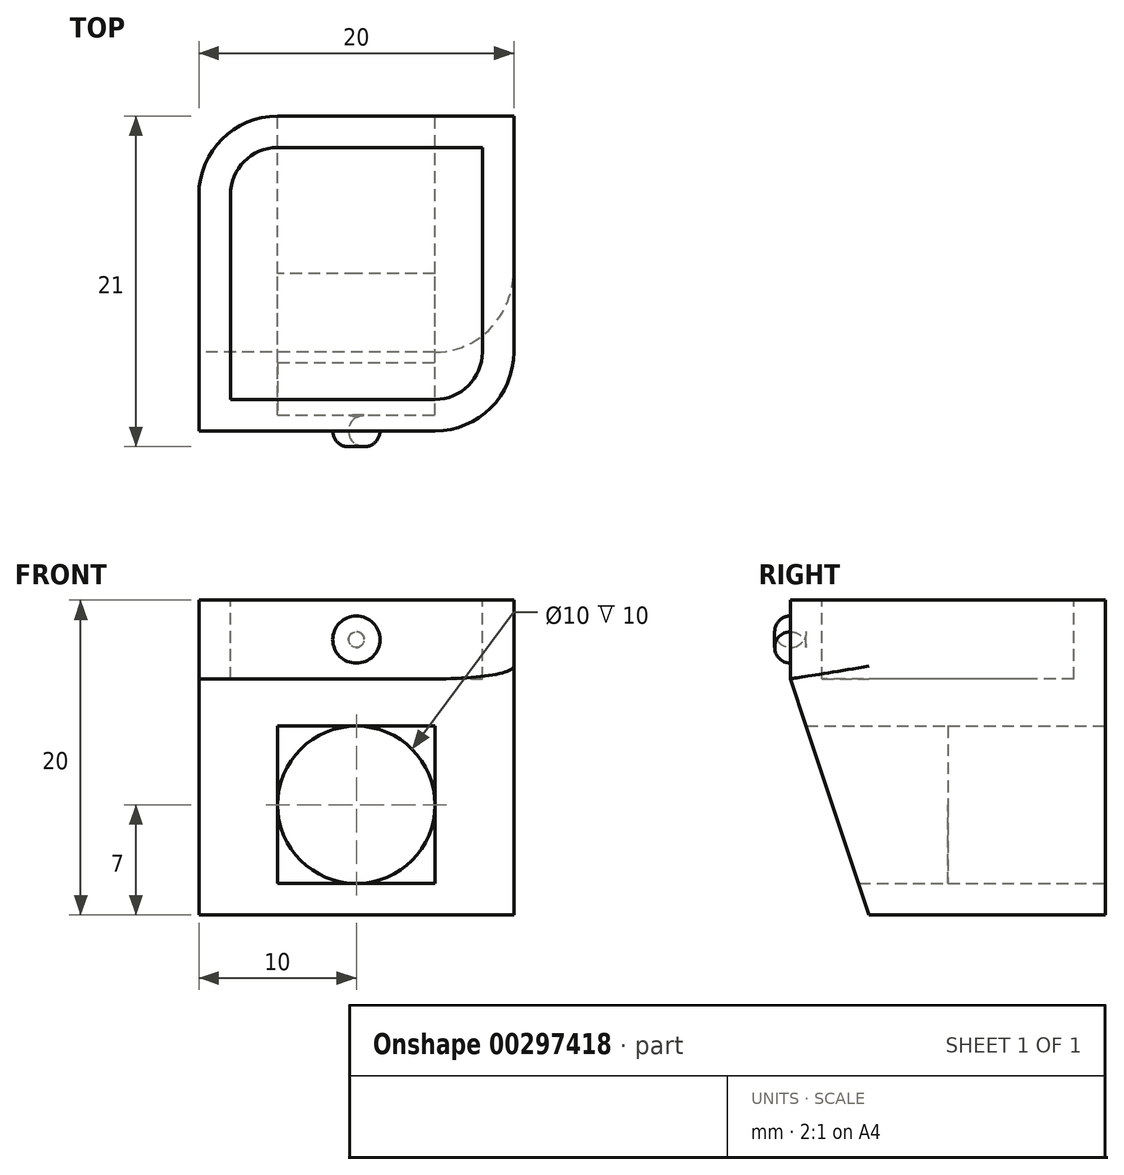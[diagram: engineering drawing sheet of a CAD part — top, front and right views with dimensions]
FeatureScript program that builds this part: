
annotation { "Feature Type Name" : "Feature", "Feature Type Description" : "" }
export const myFeature = defineFeature(function(context is Context, id is Id, definition is map)
    precondition{}
    {
        {
            var Q0;
            Q0=qCreatedBy(makeId("Top.planeOp"),FACE);
            var sketch = newSketch(context, id + "F0", { "sketchPlane" : qUnion([Q0])});
            skLineSegment(sketch, "E0.bottom", {"start": v(10, 10) * mm, "end": v(-10, 10) * mm});
            skLineSegment(sketch, "E0.top", {"start": v(10, -10) * mm, "end": v(-10, -10) * mm});
            skLineSegment(sketch, "E0.left", {"start": v(10, 10) * mm, "end": v(10, -10) * mm});
            skLineSegment(sketch, "E0.right", {"start": v(-10, 10) * mm, "end": v(-10, -10) * mm});
            skPoint(sketch, "E0.middle", {"position": v(0, 0) * mm});
            skSolve(sketch);
        }
        {
            var Q0;
            Q0 = qSketchRegion(id + "F0", true);
            extrude(context, id + "F1", {"entities" : qUnion([Q0]), "depth" : 20 * mm});
        }
        {
            var Q0;
            Q0=makeQuery(id+"F1.opExtrude","SWEPT_FACE",FACE,{"disambiguationData":[OSD([sQuery(id+"F0.wireOp",EDGE,"E0.bottom")])]});
            var sketch = newSketch(context, id + "F2", { "sketchPlane" : qUnion([Q0])});
            skCircle(sketch, "E1", {"center": v(0, 7) * mm, "radius": 5 * mm});
            skSolve(sketch);
        }
        {
            var Q0;
            Q0=makeQuery(id+"F1.opExtrude","SWEPT_FACE",FACE,{"disambiguationData":[OSD([sQuery(id+"F0.wireOp",EDGE,"E0.top")])]});
            var sketch = newSketch(context, id + "F3", { "sketchPlane" : qUnion([Q0])});
            skLineSegment(sketch, "E2.bottom", {"start": v(5, 12) * mm, "end": v(-5, 12) * mm});
            skLineSegment(sketch, "E2.top", {"start": v(5, 2) * mm, "end": v(-5, 2) * mm});
            skLineSegment(sketch, "E2.left", {"start": v(5, 12) * mm, "end": v(5, 2) * mm});
            skLineSegment(sketch, "E2.right", {"start": v(-5, 12) * mm, "end": v(-5, 2) * mm});
            skPoint(sketch, "E2.middle", {"position": v(0, 7) * mm});
            skSolve(sketch);
        }
        {
            var Q0;
            Q0=qCreatedBy(makeId("Front.planeOp"),FACE);
            var sketch = newSketch(context, id + "F4", { "sketchPlane" : qUnion([Q0])});
            skLineSegment(sketch, "E3.0", {"start": v(5, 12) * mm, "end": v(-5, 12) * mm});
            skLineSegment(sketch, "E4.0", {"start": v(-5, 12) * mm, "end": v(-5, 2) * mm});
            skLineSegment(sketch, "E5.0", {"start": v(5, 2) * mm, "end": v(-5, 2) * mm});
            skLineSegment(sketch, "E6.0", {"start": v(5, 12) * mm, "end": v(5, 2) * mm});
            skSolve(sketch);
        }
        {
            var Q0;
            Q0=makeQuery(id+"F1.opExtrude","CAP_EDGE",EDGE,{"disambiguationData":[OSD([sQuery(id+"F0.wireOp",EDGE,"E0.top")])],"isStart":true});
            chamfer(context, id + "F5", {"entities" : qUnion([Q0]), "chamferType" : ChamferType.TWO_OFFSETS, "width1" : 15 * mm, "oppositeDirection" : true, "width2" : 5 * mm, "tangentPropagation" : true});
        }
        {
            var Q0;
            Q0=makeQuery(id+"F1.opExtrude","SWEPT_EDGE",EDGE,{"disambiguationData":[OSD([sQuery(id+"F0.wireOp",EDGE,"E0.bottom"),sQuery(id+"F0.wireOp",EDGE,"E0.right")])]});
            var Q1;
            Q1=makeQuery(id+"F1.opExtrude","SWEPT_EDGE",EDGE,{"disambiguationData":[OSD([sQuery(id+"F0.wireOp",EDGE,"E0.top"),sQuery(id+"F0.wireOp",EDGE,"E0.left")])]});
            var Q2;
            Q2=makeQuery(id+"F5.opChamfer","BLEND_EDGE",EDGE,{"blendedFrom":[makeQuery(id+"F1.opExtrude","CAP_EDGE",EDGE,{"disambiguationData":[OSD([sQuery(id+"F0.wireOp",EDGE,"E0.top")])],"isStart":true}),makeQuery(id+"F1.opExtrude","SWEPT_FACE",FACE,{"disambiguationData":[OSD([sQuery(id+"F0.wireOp",EDGE,"E0.left")])]})],"blendedInto":[makeQuery(id+"F1.opExtrude","SWEPT_FACE",FACE,{"disambiguationData":[OSD([sQuery(id+"F0.wireOp",EDGE,"E0.left")])]})]});
            fillet(context, id + "F6", {"entities" : qUnion([Q0, Q1, Q2]), "radius" : 5 * mm, "tangentPropagation" : true, "allowEdgeOverflow" : false});
        }
        {
            var Q0;
            Q0=makeQuery(id+"F1.opExtrude","CAP_FACE",FACE,{"disambiguationData":[OSD([sQuery(id+"F0.wireOp",EDGE,"E0.bottom"),sQuery(id+"F0.wireOp",EDGE,"E0.top"),sQuery(id+"F0.wireOp",EDGE,"E0.left"),sQuery(id+"F0.wireOp",EDGE,"E0.right")])],"isStart":false});
            var sketch = newSketch(context, id + "F7", { "sketchPlane" : qUnion([Q0])});
            skLineSegment(sketch, "E7.0", {"start": v(5, -8) * mm, "end": v(-8, -8) * mm});
            skLineSegment(sketch, "E7.1", {"start": v(8, 8) * mm, "end": v(8, -5) * mm});
            skLineSegment(sketch, "E7.2", {"start": v(8, 8) * mm, "end": v(-5, 8) * mm});
            skArc(sketch, "E7.3", {"start": v(5, -8) * mm, "mid": v(7.12, -7.12) * mm, "end": v(8, -5) * mm});
            skArc(sketch, "E7.4", {"start": v(-5, 8) * mm, "mid": v(-7.12, 7.12) * mm, "end": v(-8, 5) * mm});
            skLineSegment(sketch, "E7.5", {"start": v(-8, 5) * mm, "end": v(-8, -8) * mm});
            skSolve(sketch);
        }
        {
            var Q0;
            Q0 = qSketchRegion(id + "F7", true);
            extrude(context, id + "F8", {"entities" : qUnion([Q0]), "operationType" : NewBodyOperationType.REMOVE, "oppositeDirection" : true, "depth" : 5 * mm});
        }
        {
            var Q0;
            Q0=makeQuery(id+"F1.opExtrude","SWEPT_FACE",FACE,{"disambiguationData":[OSD([sQuery(id+"F0.wireOp",EDGE,"E0.top")])]});
            var sketch = newSketch(context, id + "F9", { "sketchPlane" : qUnion([Q0])});
            skCircle(sketch, "E8", {"center": v(0, 17.5) * mm, "radius": 1.5 * mm});
            skSolve(sketch);
        }
        {
            var Q0;
            Q0 = qSketchRegion(id + "F9", true);
            extrude(context, id + "F10", {"entities" : qUnion([Q0]), "operationType" : NewBodyOperationType.REMOVE, "oppositeDirection" : true, "depth" : 1 * mm});
        }
        {
            var Q0;
            Q0=makeQuery(id+"F10.boolean.opBoolean","COPY",EDGE,{"derivedFrom":makeQuery(id+"F10.opExtrude","CAP_EDGE",EDGE,{"disambiguationData":[OSD([sQuery(id+"F9.wireOp",EDGE,"E8")])],"isStart":false})});
            fillet(context, id + "F11", {"entities" : qUnion([Q0]), "radius" : 1 * mm, "tangentPropagation" : true, "allowEdgeOverflow" : false});
        }
        {
            var Q0;
            Q0=qCreatedBy(makeId("Front.planeOp"),FACE);
            var sketch = newSketch(context, id + "F12", { "sketchPlane" : qUnion([Q0])});
            skLineSegment(sketch, "E9", {"start": v(0, 0) * mm, "end": v(0, 27.76) * mm});
            skSolve(sketch);
        }
        {
            var Q0;
            Q0 = qSketchRegion(id + "F7", true);
            extrude(context, id + "F13", {"entities" : qUnion([Q0]), "operationType" : NewBodyOperationType.REMOVE, "oppositeDirection" : true, "depth" : 5 * mm});
        }
        {
            var Q0;
            Q0 = qSketchRegion(id + "F2", true);
            extrude(context, id + "F14", {"entities" : qUnion([Q0]), "operationType" : NewBodyOperationType.REMOVE, "endBound" : BoundingType.THROUGH_ALL, "oppositeDirection" : true, "depth" : 25 * mm});
        }
        {
            var Q0;
            Q0 = qSketchRegion(id + "F4", true);
            extrude(context, id + "F15", {"entities" : qUnion([Q0]), "operationType" : NewBodyOperationType.REMOVE, "depth" : 25 * mm});
        }
    });
